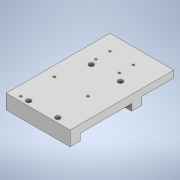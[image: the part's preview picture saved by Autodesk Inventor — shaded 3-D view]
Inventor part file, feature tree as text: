
AUTODESK INVENTOR PART (.ipt)
format: ipt  version: 2020 (Build 240168000, 168)  size: 161,280 bytes
history: native  units: mm
features: sketch x5, extrude x3, hole x3
ambient origin geometry x8: Origin, YZ Plane, XZ Plane, XY Plane, X Axis, Y Axis, Z Axis, Center Point
bodies: Solid1 (feature_tree)
feature tree (11):
  extrude  "Extrusion1"  Depth=64.0mm
  sketch  "Sketch2"  dims[d2=7.0mm d3=0.0mm d4=26.0mm]
  extrude  "Extrusion2"  Depth=7.0mm
  hole  "Hole1"  [1 undecoded]
  hole  "Hole2"  [1 undecoded]
  extrude  "Extrusion3"  Depth=6.0mm
  hole  "Hole3"  [1 undecoded]
  sketch  "Sketch1"  dims[d0=57.0mm d1=64.0mm]
  sketch  "Sketch3"  dims[d5=16.0mm d6=4.0mm]
  sketch  "Sketch5"  dims[d7=4.0mm d8=4.0mm]
  sketch  "Sketch6"  dims[d9=4.0mm d10=26.0mm d11=16.0mm d12=9.0mm d13=9.0mm d14=6.0mm d15=0.0mm d16=4.3mm d17=6.0mm d18=4.0mm d19=2.0mm d20=90.0deg d21=8.0mm d22=20.594885mm d28=4.0mm d30=9.0mm d33=2.05mm d34=6.0mm d35=4.0mm d36=2.0mm d37=90.0deg d38=8.0mm d39=20.594885mm d41=30.0mm d42=30.0mm d43=6.0mm d44=28.63mm d45=0.0mm d46=21.0mm d47=66.0mm d48=22.0mm d49=12.5mm d50=1.9mm d51=6.0mm d52=4.0mm d53=2.0mm d54=90.0deg d55=8.0mm d56=20.594885mm]
note: 3 required parameter values undecoded (feature->parameter linkage not recoverable at this tier; creation-order binding heuristic only, values carry confidence <= 0.55)
